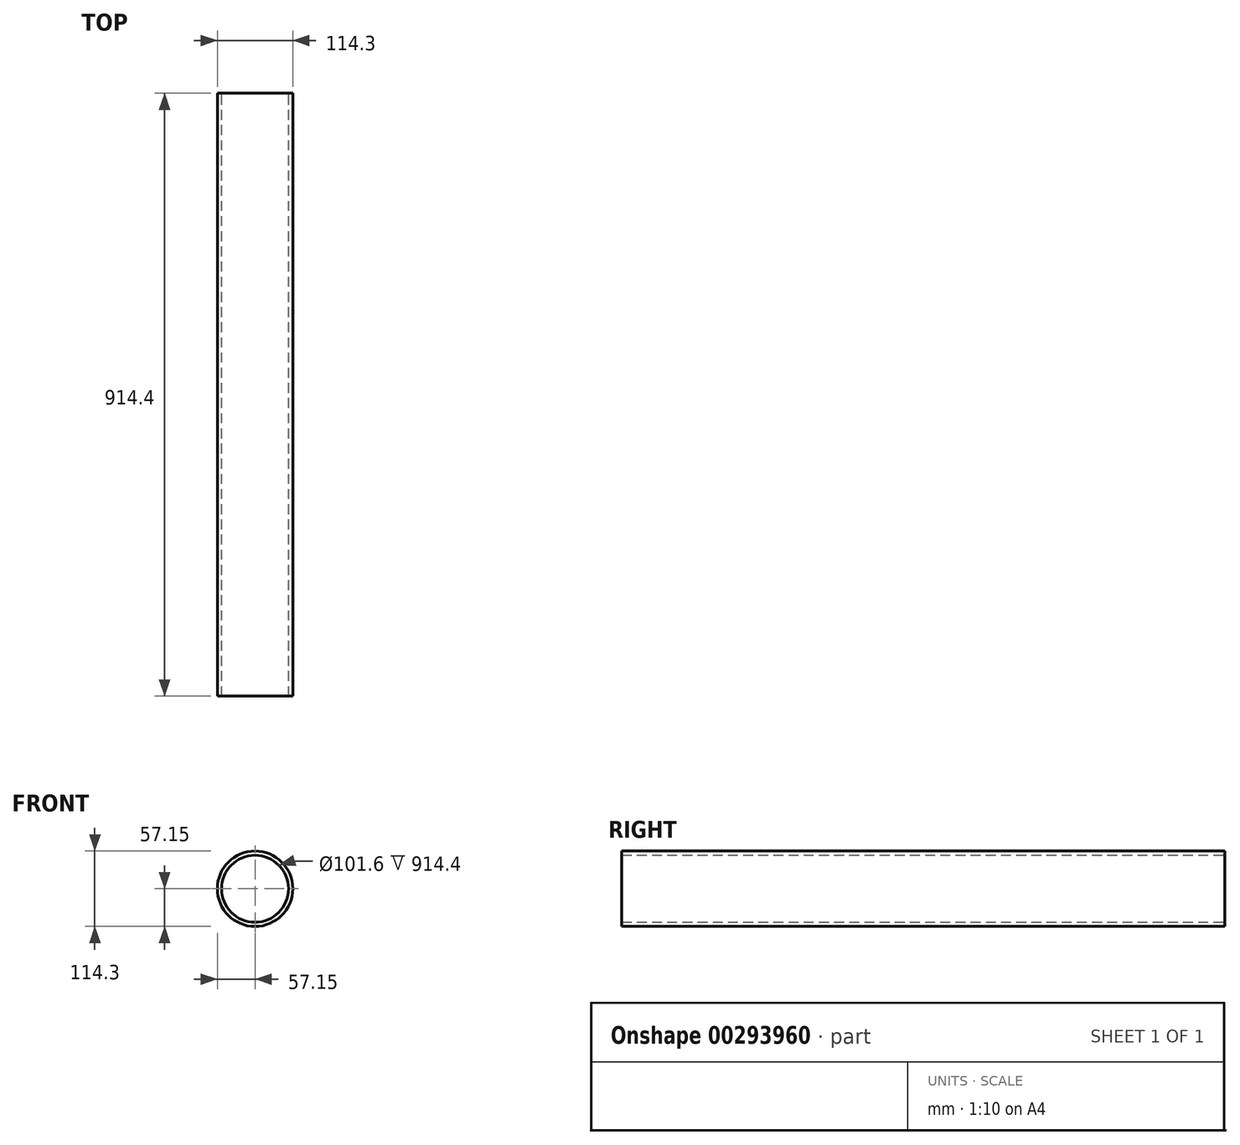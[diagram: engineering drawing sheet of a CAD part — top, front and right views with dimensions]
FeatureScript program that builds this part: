
annotation { "Feature Type Name" : "Feature", "Feature Type Description" : "" }
export const myFeature = defineFeature(function(context is Context, id is Id, definition is map)
    precondition{}
    {
        {
            var Q0;
            Q0=qCreatedBy(makeId("Front.planeOp"),FACE);
            var sketch = newSketch(context, id + "F0", { "sketchPlane" : qUnion([Q0])});
            skCircle(sketch, "E0", {"center": v(0, 0) * mm, "radius": 50.8 * mm});
            skCircle(sketch, "E1", {"center": v(0, 0) * mm, "radius": 57.15 * mm});
            skSolve(sketch);
        }
        {
            var Q0;
            Q0 = qSketchRegion(id + "F0", true);
            extrude(context, id + "F1", {"entities" : qUnion([Q0]), "depth" : 914.4 * mm, "offsetDistance" : 25 * mm, "symmetric" : true});
        }
    });
